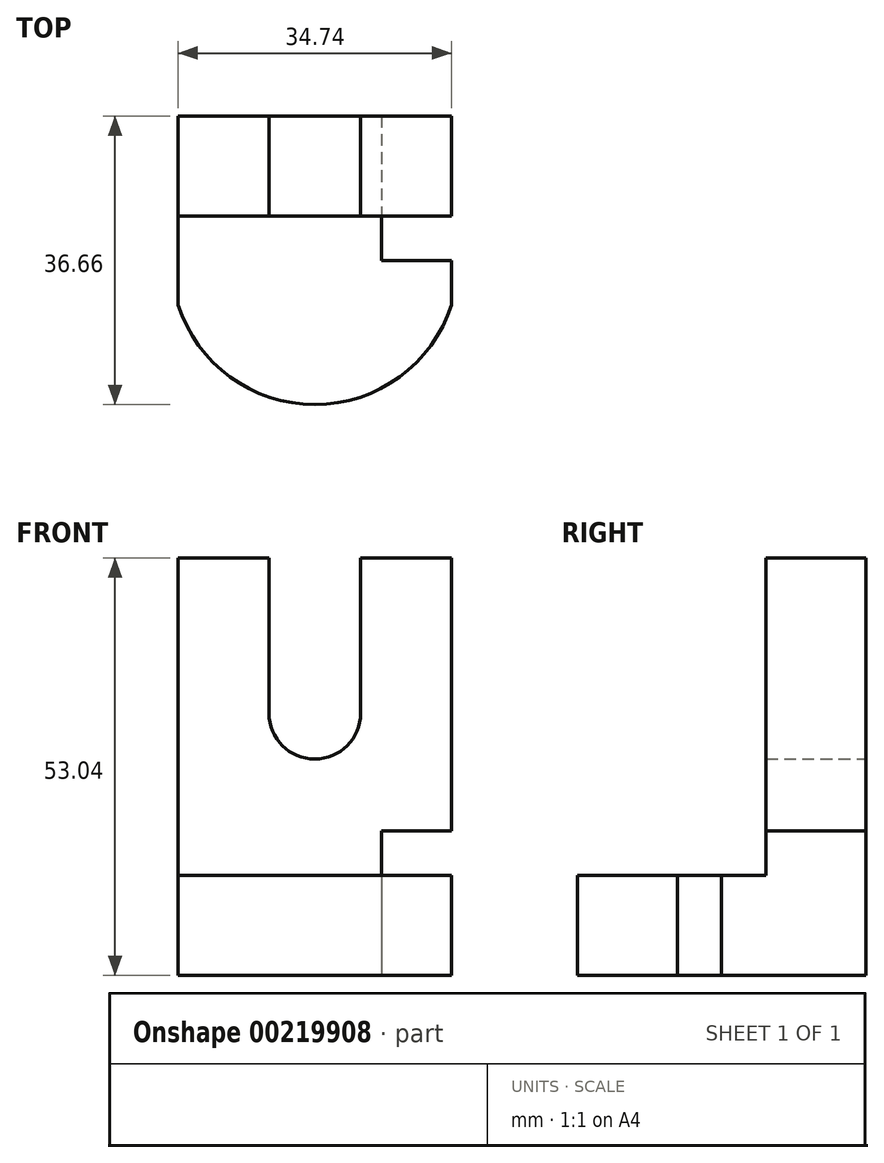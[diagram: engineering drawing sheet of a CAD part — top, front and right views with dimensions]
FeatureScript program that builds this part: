
annotation { "Feature Type Name" : "Feature", "Feature Type Description" : "" }
export const myFeature = defineFeature(function(context is Context, id is Id, definition is map)
    precondition{}
    {
        {
            var Q0;
            Q0=qCreatedBy(makeId("Top.planeOp"),FACE);
            var sketch = newSketch(context, id + "F0", { "sketchPlane" : qUnion([Q0])});
            skLineSegment(sketch, "E0", {"start": v(0, 0) * mm, "end": v(-34.74, 0) * mm});
            skLineSegment(sketch, "E1", {"start": v(-34.74, 0) * mm, "end": v(-34.74, -24) * mm});
            skLineSegment(sketch, "E2", {"start": v(0, 0) * mm, "end": v(0, -24) * mm});
            skArc(sketch, "E3", {"start": v(-34.74, -24) * mm, "mid": v(-17.37, -36.66) * mm, "end": v(0, -24) * mm});
            skSolve(sketch);
        }
        {
            var Q0;
            Q0=makeQuery(id+"F0.imprint","IMPRINT",FACE,{"disambiguationData":[TD([[makeQuery(id+"F0.imprint","IMPRINT",EDGE,{"derivedFrom":sQuery(id+"F0.wireOp",EDGE,"E0")}),1.0]])]});
            extrude(context, id + "F1", {"entities" : qUnion([Q0]), "depth" : 12.7 * mm});
        }
        {
            var Q0;
            Q0=qCreatedBy(makeId("Front.planeOp"),FACE);
            var sketch = newSketch(context, id + "F2", { "sketchPlane" : qUnion([Q0])});
            skPoint(sketch, "E4.0", {"position": v(0, 12.7) * mm});
            skPoint(sketch, "E5.0", {"position": v(-34.74, 12.7) * mm});
            skPoint(sketch, "E6.0", {"position": v(-17.37, 12.7) * mm});
            skLineSegment(sketch, "E7", {"start": v(-34.74, 12.7) * mm, "end": v(-34.74, 53.04) * mm});
            skLineSegment(sketch, "E8", {"start": v(0, 12.7) * mm, "end": v(0, 53.04) * mm});
            skLineSegment(sketch, "E9", {"start": v(0, 53.04) * mm, "end": v(-11.55, 53.04) * mm});
            skLineSegment(sketch, "E10", {"start": v(-34.74, 53.04) * mm, "end": v(-23.19, 53.04) * mm});
            skLineSegment(sketch, "E11", {"start": v(-23.19, 53.04) * mm, "end": v(-23.19, 33.31) * mm});
            skLineSegment(sketch, "E12", {"start": v(-11.55, 53.04) * mm, "end": v(-11.55, 33.31) * mm});
            skArc(sketch, "E13", {"start": v(-23.19, 33.31) * mm, "mid": v(-17.37, 27.5) * mm, "end": v(-11.55, 33.31) * mm});
            skLineSegment(sketch, "E14", {"start": v(0, 12.7) * mm, "end": v(-34.74, 12.7) * mm});
            skSolve(sketch);
        }
        {
            var Q0;
            Q0=makeQuery(id+"F2.imprint","IMPRINT",FACE,{"disambiguationData":[TD([[makeQuery(id+"F2.imprint","IMPRINT",EDGE,{"derivedFrom":sQuery(id+"F2.wireOp",EDGE,"E7")}),-1.0]])]});
            extrude(context, id + "F3", {"entities" : qUnion([Q0]), "operationType" : NewBodyOperationType.ADD, "depth" : 12.7 * mm});
        }
        {
            var Q0;
            Q0=makeQuery(id+"F3.boolean.opBoolean","MERGE",FACE,{"derivedFrom":[makeQuery(id+"F1.opExtrude","SWEPT_FACE",FACE,{"disambiguationData":[OSD([sQuery(id+"F0.wireOp",EDGE,"E2")])]}),makeQuery(id+"F3.opExtrude","SWEPT_FACE",FACE,{"disambiguationData":[OSD([sQuery(id+"F2.wireOp",EDGE,"E8")])]})]});
            var sketch = newSketch(context, id + "F4", { "sketchPlane" : qUnion([Q0])});
            skLineSegment(sketch, "E15", {"start": v(0, 0) * mm, "end": v(0, 18.35) * mm});
            skLineSegment(sketch, "E16", {"start": v(0, 18.35) * mm, "end": v(-12.7, 18.35) * mm});
            skLineSegment(sketch, "E17", {"start": v(-12.7, 18.35) * mm, "end": v(-12.7, 12.7) * mm});
            skLineSegment(sketch, "E18", {"start": v(-12.7, 12.7) * mm, "end": v(-18.35, 12.7) * mm});
            skLineSegment(sketch, "E19", {"start": v(-18.35, 12.7) * mm, "end": v(-18.35, 0) * mm});
            skLineSegment(sketch, "E20", {"start": v(-18.35, 0) * mm, "end": v(0, 0) * mm});
            skSolve(sketch);
        }
        {
            var Q0;
            Q0=makeQuery(id+"F4.imprint","IMPRINT",FACE,{"disambiguationData":[TD([[makeQuery(id+"F4.imprint","IMPRINT",EDGE,{"derivedFrom":sQuery(id+"F4.wireOp",EDGE,"E15")}),-1.0]])]});
            extrude(context, id + "F5", {"entities" : qUnion([Q0]), "operationType" : NewBodyOperationType.REMOVE, "oppositeDirection" : true, "depth" : 8.9 * mm});
        }
    });
